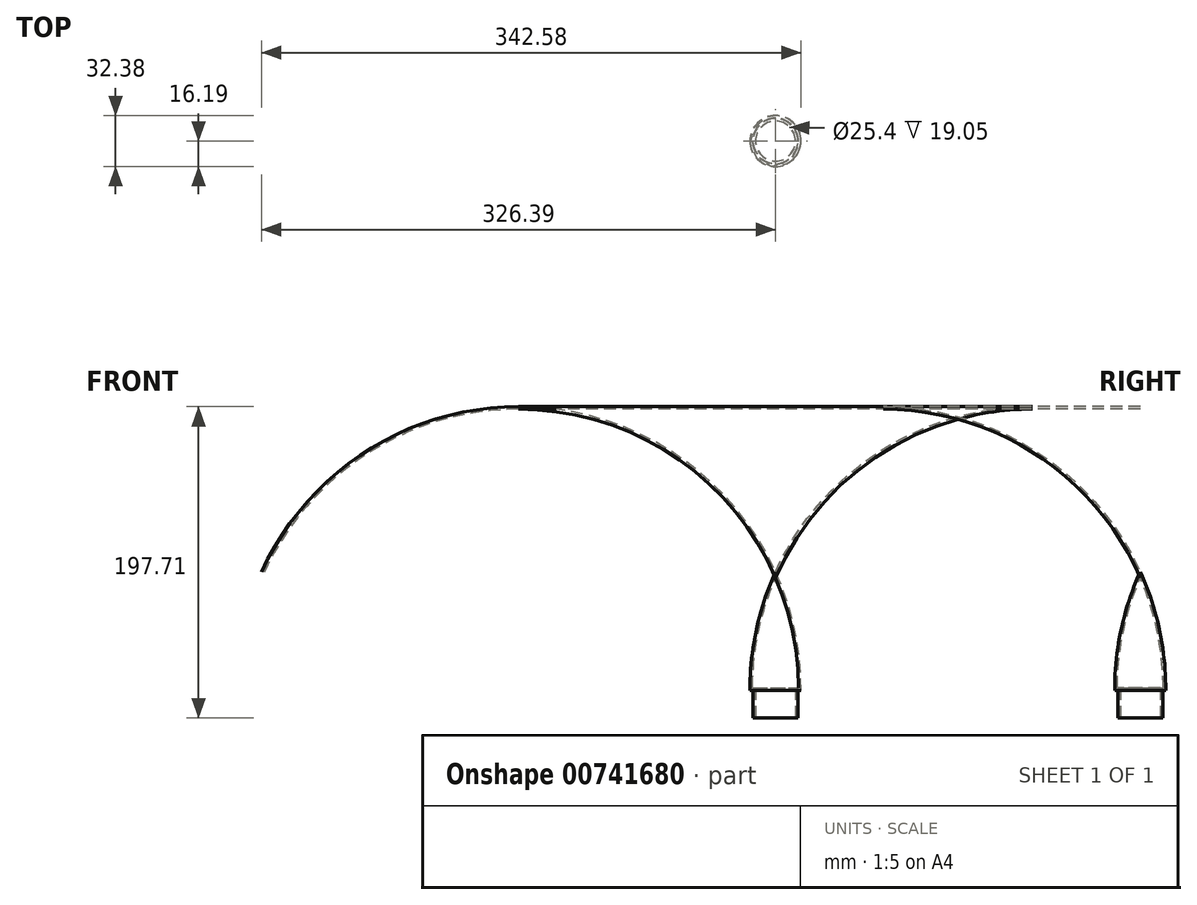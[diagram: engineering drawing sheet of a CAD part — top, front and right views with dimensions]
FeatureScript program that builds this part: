
annotation { "Feature Type Name" : "Feature", "Feature Type Description" : "" }
export const myFeature = defineFeature(function(context is Context, id is Id, definition is map)
    precondition{}
    {
        {
            var Q0;
            Q0=qCreatedBy(makeId("Front.planeOp"),FACE);
            var sketch = newSketch(context, id + "F0", { "sketchPlane" : qUnion([Q0])});
            skLineSegment(sketch, "E0", {"start": v(0, 0) * mm, "end": v(0, 88.9) * mm});
            skLineSegment(sketch, "E1", {"start": v(0, 0) * mm, "end": v(12.7, 0) * mm});
            skLineSegment(sketch, "E2", {"start": v(12.7, 0) * mm, "end": v(12.7, 19.05) * mm});
            skLineSegment(sketch, "E3", {"start": v(12.7, 19.05) * mm, "end": v(14.6, 19.05) * mm});
            skArc(sketch, "E4", {"start": v(14.6, 19.05) * mm, "mid": v(10.84, 54.72) * mm, "end": v(0, 88.9) * mm});
            skArc(sketch, "E5.0", {"start": v(16.2, 17.46) * mm, "mid": v(12.19, 56.02) * mm, "end": v(0, 92.8) * mm});
            skLineSegment(sketch, "E5.1", {"start": v(14.29, 17.46) * mm, "end": v(16.2, 17.46) * mm});
            skLineSegment(sketch, "E5.2", {"start": v(14.29, 0) * mm, "end": v(14.29, 17.46) * mm});
            skLineSegment(sketch, "E6", {"start": v(14.29, 0) * mm, "end": v(12.7, 0) * mm});
            skLineSegment(sketch, "E7", {"start": v(0, 88.9) * mm, "end": v(0, 92.8) * mm});
            skSolve(sketch);
        }
        {
            var Q0;
            Q0=makeQuery(id+"F0.imprint","IMPRINT",FACE,{"disambiguationData":[TD([[makeQuery(id+"F0.imprint","IMPRINT",EDGE,{"derivedFrom":sQuery(id+"F0.wireOp",EDGE,"E2")}),-1.0]])]});
            var Q1;
            Q1=sQuery(id+"F0.wireOp",EDGE,"E0");
            revolve(context, id + "F1", {"surfaceOperationType" : NewSurfaceOperationType.NEW, "entities" : qUnion([Q0]), "axis" : qUnion([Q1]), "revolveType" : RevolveType.FULL});
        }
    });
